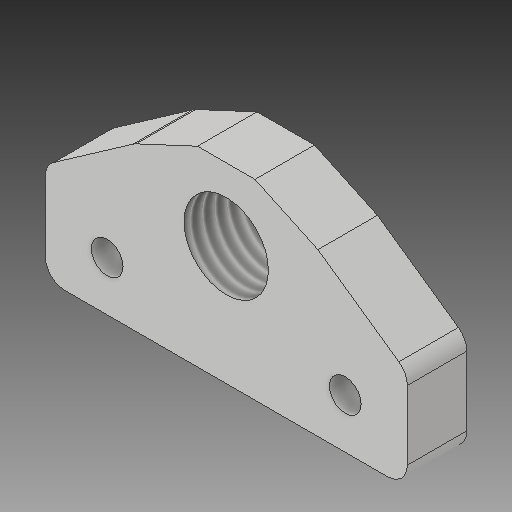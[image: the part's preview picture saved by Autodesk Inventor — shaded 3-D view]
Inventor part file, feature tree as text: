
AUTODESK INVENTOR PART (.ipt)
format: ipt  version: 2018 (Build 220112000, 112)  size: 125,440 bytes
history: native  units: mm
features: extrude x1, thread x1, sketch x1
ambient origin geometry x8: Origin, YZ Plane, XZ Plane, XY Plane, X Axis, Y Axis, Z Axis, Center Point
bodies: Solid1 (feature_tree)
feature tree (3):
  extrude  "Extrusion1"  Depth=10.0mm TaperAngle=0.0deg
  thread  "Thread1"  [1 undecoded]
  sketch  "Sketch1"  dims[d0=6.0mm d1=0.0mm d2=10.0mm d3=0.0mm]
note: 1 required parameter value undecoded (feature->parameter linkage not recoverable at this tier; creation-order binding heuristic only, values carry confidence <= 0.55)
